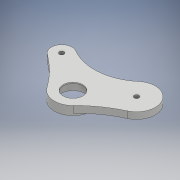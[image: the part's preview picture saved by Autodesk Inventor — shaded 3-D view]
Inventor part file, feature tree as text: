
AUTODESK INVENTOR PART (.ipt)
format: ipt  version: 2017 (Build 210142000, 142)  size: 291,328 bytes
history: native  units: mm
features: extrude x3, sketch x3
ambient origin geometry x8: Origin, YZ Plane, XZ Plane, XY Plane, X Axis, Y Axis, Z Axis, Center Point
bodies: Solid1 (feature_tree)
feature tree (6):
  extrude  "Extrusion1"  Depth=4.3mm
  extrude  "Extrusion2"  Depth=34.0mm
  extrude  "Extrusion3"  Depth=17.0mm
  sketch  "Sketch1"  dims[d0=22.0mm d1=4.3mm]
  sketch  "Sketch2"  dims[d2=4.3mm d4=34.0mm]
  sketch  "Sketch3"  dims[d5=34.6mm d6=7.2mm d8=6.0mm d9=80.0mm d10=6.0mm d11=0.0mm d12=8.0mm d13=0.0mm d16=24.3mm d17=24.0mm d18=1.0mm d19=0.0mm d20=17.0mm d21=18.0mm]
